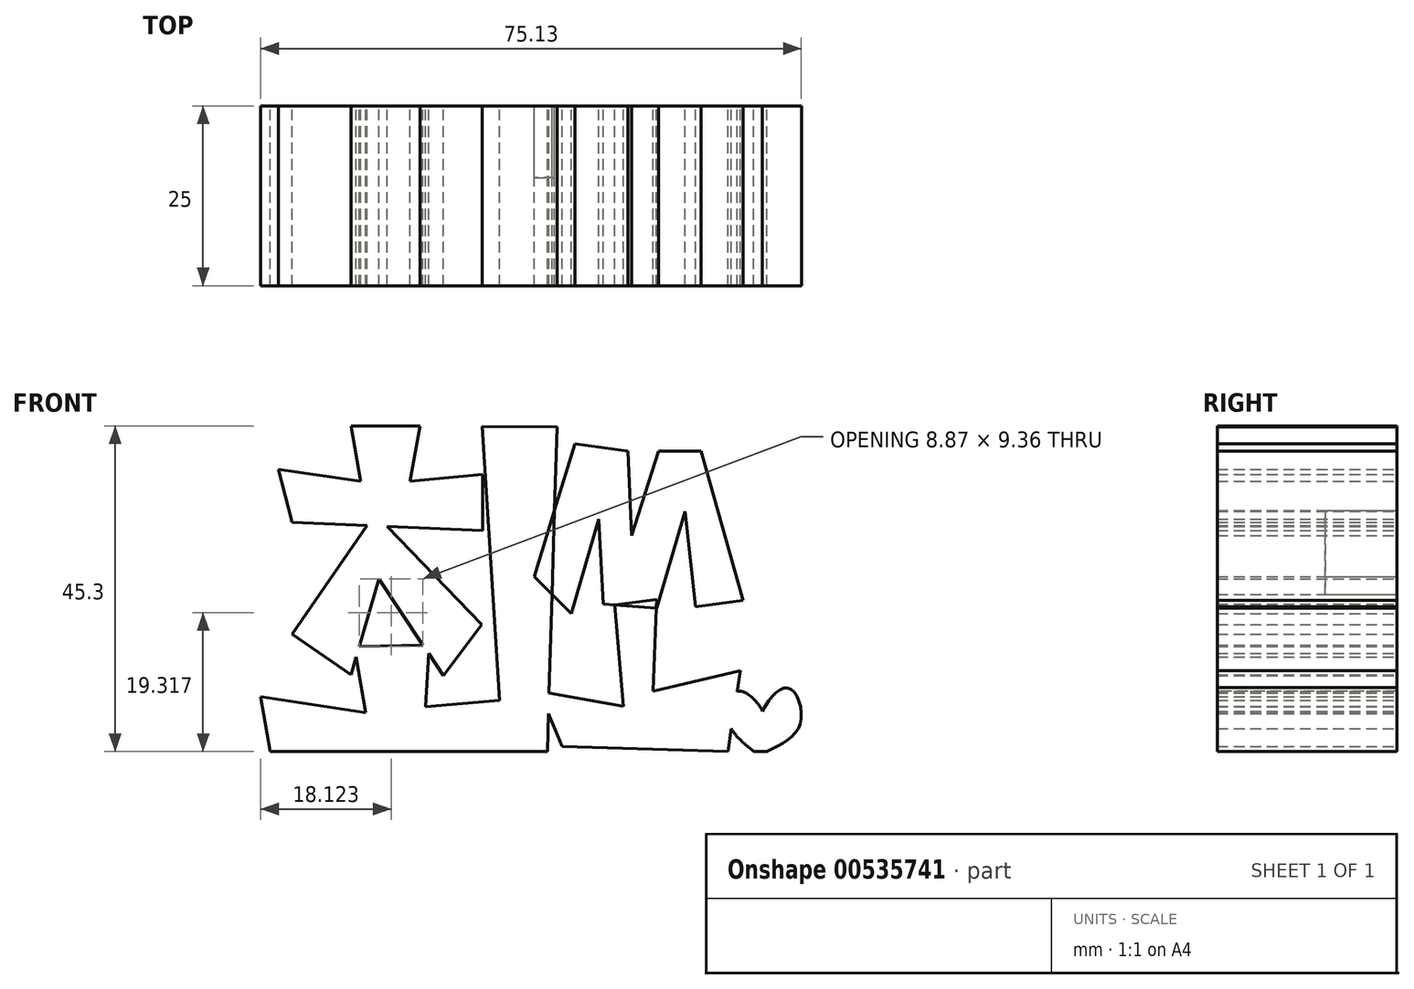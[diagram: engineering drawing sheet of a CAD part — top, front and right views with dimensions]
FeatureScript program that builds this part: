
annotation { "Feature Type Name" : "Feature", "Feature Type Description" : "" }
export const myFeature = defineFeature(function(context is Context, id is Id, definition is map)
    precondition{}
    {
        {
            var Q0;
            Q0=qCreatedBy(makeId("Front.planeOp"),FACE);
            var sketch = newSketch(context, id + "F0", { "sketchPlane" : qUnion([Q0])});
            skLineSegment(sketch, "E0", {"start": v(-41.35, 31.22) * mm, "end": v(-31.75, 31.22) * mm});
            skLineSegment(sketch, "E1", {"start": v(-31.75, 31.22) * mm, "end": v(-33.15, 23.5) * mm});
            skLineSegment(sketch, "E2", {"start": v(-33.15, 23.5) * mm, "end": v(-23.06, 24.46) * mm});
            skLineSegment(sketch, "E3", {"start": v(-23.06, 24.46) * mm, "end": v(-23.06, 16.67) * mm});
            skLineSegment(sketch, "E4", {"start": v(-23.06, 16.67) * mm, "end": v(-49.5, 17.8) * mm});
            skLineSegment(sketch, "E5", {"start": v(-49.5, 17.8) * mm, "end": v(-51.41, 25.15) * mm});
            skLineSegment(sketch, "E6", {"start": v(-51.41, 25.15) * mm, "end": v(-40, 23.5) * mm});
            skLineSegment(sketch, "E7", {"start": v(-40, 23.5) * mm, "end": v(-41.35, 31.22) * mm});
            skLineSegment(sketch, "E8", {"start": v(-39.09, 17.35) * mm, "end": v(-49.5, 2.24) * mm});
            skLineSegment(sketch, "E9", {"start": v(-49.5, 2.24) * mm, "end": v(-41.35, -3.39) * mm});
            skLineSegment(sketch, "E10", {"start": v(-41.35, -3.39) * mm, "end": v(-37.44, 9.92) * mm});
            skLineSegment(sketch, "E11", {"start": v(-37.44, 9.92) * mm, "end": v(-28.48, -3.52) * mm});
            skLineSegment(sketch, "E12", {"start": v(-28.48, -3.52) * mm, "end": v(-23.19, 3.56) * mm});
            skLineSegment(sketch, "E13", {"start": v(-23.19, 3.56) * mm, "end": v(-36.28, 17.23) * mm});
            skLineSegment(sketch, "E14", {"start": v(-40.63, -0.95) * mm, "end": v(-39.27, -8.71) * mm});
            skLineSegment(sketch, "E15", {"start": v(-39.27, -8.71) * mm, "end": v(-53.88, -6.46) * mm});
            skLineSegment(sketch, "E16", {"start": v(-53.88, -6.46) * mm, "end": v(-52.55, -14.08) * mm});
            skLineSegment(sketch, "E17", {"start": v(-52.55, -14.08) * mm, "end": v(-17.7, -14.08) * mm});
            skLineSegment(sketch, "E18", {"start": v(-17.7, -14.08) * mm, "end": v(-19.06, -6.8) * mm});
            skLineSegment(sketch, "E19", {"start": v(-19.06, -6.8) * mm, "end": v(-30.99, -7.88) * mm});
            skLineSegment(sketch, "E20", {"start": v(-30.99, -7.88) * mm, "end": v(-30.45, 0.76) * mm});
            skLineSegment(sketch, "E21", {"start": v(-30.45, 0.76) * mm, "end": v(-41.04, 0.54) * mm});
            skLineSegment(sketch, "E22", {"start": v(-41.04, 0.54) * mm, "end": v(-40.63, -0.95) * mm});
            skLineSegment(sketch, "E23", {"start": v(-23.12, 31.16) * mm, "end": v(-20.2, -14.08) * mm});
            skLineSegment(sketch, "E24", {"start": v(-20.2, -14.08) * mm, "end": v(-14.05, -14.08) * mm});
            skLineSegment(sketch, "E25", {"start": v(-14.05, -14.08) * mm, "end": v(-12.7, 31.07) * mm});
            skLineSegment(sketch, "E26", {"start": v(-12.7, 31.07) * mm, "end": v(-23.12, 31.16) * mm});
            skLineSegment(sketch, "E27", {"start": v(-10.2, 28.7) * mm, "end": v(-15.86, 10.26) * mm});
            skLineSegment(sketch, "E28", {"start": v(-15.86, 10.26) * mm, "end": v(-10.73, 5.12) * mm});
            skLineSegment(sketch, "E29", {"start": v(-10.73, 5.12) * mm, "end": v(-6.89, 18.24) * mm});
            skLineSegment(sketch, "E30", {"start": v(-6.89, 18.24) * mm, "end": v(-6.25, 6.4) * mm});
            skLineSegment(sketch, "E31", {"start": v(-6.25, 6.4) * mm, "end": v(1.14, 5.85) * mm});
            skLineSegment(sketch, "E32", {"start": v(1.14, 5.85) * mm, "end": v(5.08, 19.3) * mm});
            skLineSegment(sketch, "E33", {"start": v(5.08, 19.3) * mm, "end": v(6.55, 6.08) * mm});
            skLineSegment(sketch, "E34", {"start": v(6.55, 6.08) * mm, "end": v(13.16, 6.93) * mm});
            skLineSegment(sketch, "E35", {"start": v(13.16, 6.93) * mm, "end": v(7.3, 27.73) * mm});
            skLineSegment(sketch, "E36", {"start": v(7.3, 27.73) * mm, "end": v(1.43, 27.73) * mm});
            skLineSegment(sketch, "E37", {"start": v(1.43, 27.73) * mm, "end": v(-2.31, 15.93) * mm});
            skLineSegment(sketch, "E38", {"start": v(-2.31, 15.93) * mm, "end": v(-2.84, 27.73) * mm});
            skLineSegment(sketch, "E39", {"start": v(-2.84, 27.73) * mm, "end": v(-10.2, 28.7) * mm});
            skLineSegment(sketch, "E40", {"start": v(-4.67, 6.29) * mm, "end": v(1.14, 7.06) * mm});
            skLineSegment(sketch, "E41", {"start": v(1.14, 7.06) * mm, "end": v(0.67, -5.71) * mm});
            skLineSegment(sketch, "E42", {"start": v(0.67, -5.71) * mm, "end": v(12.76, -2.85) * mm});
            skLineSegment(sketch, "E43", {"start": v(12.76, -2.85) * mm, "end": v(11.05, -14.08) * mm});
            skLineSegment(sketch, "E44", {"start": v(11.05, -14.08) * mm, "end": v(-12, -13.38) * mm});
            skLineSegment(sketch, "E45", {"start": v(-12, -13.38) * mm, "end": v(-15.19, -5.71) * mm});
            skLineSegment(sketch, "E46", {"start": v(-15.19, -5.71) * mm, "end": v(-3.48, -7.79) * mm});
            skLineSegment(sketch, "E47", {"start": v(-3.48, -7.79) * mm, "end": v(-4.67, 6.29) * mm});
            skPoint(sketch, "E48.3.internal.snap0", {"position": v(11.9, -8.46) * mm});
            skFitSpline(sketch, "E48", {"points": [v(14.65, -14.08) * mm, v(11.05, -9.64) * mm, v(12.32, -5.74) * mm, v(15.85, -8.46) * mm, v(16.46, -14.08) * mm], "startDerivative": vector(-17.92, 14.39) * mm, "endDerivative": vector(-1.7, -21.54) * mm});
            skFitSpline(sketch, "E49", {"points": [v(14.65, -14.08) * mm, v(15.85, -8.46) * mm, v(19.47, -5.26) * mm, v(21.13, -10.1) * mm, v(16.46, -14.08) * mm], "startDerivative": vector(1.53, 21.63) * mm, "endDerivative": vector(-23.6, -11.26) * mm});
            skLineSegment(sketch, "E50", {"start": v(14.65, -14.08) * mm, "end": v(16.46, -14.08) * mm});
            skSolve(sketch);
        }
        {
            var Q0;
            {var subQ7=sQuery(id+"F0.wireOp",EDGE,"E42");Q0=makeQuery(id+"F0.imprint","IMPRINT",FACE,{"disambiguationData":[TD([[makeQuery(id+"F0.imprint","IMPRINT",EDGE,{"derivedFrom":subQ7}),-1.0]])]});}
            var Q1;
            {var subQ0=sQuery(id+"F0.wireOp",EDGE,"E48");var subQ1=sQuery(id+"F0.wireOp",EDGE,"E43");var subQ2=makeQuery(id+"F0.imprint","INTERSECT",VERTEX,{"disambiguationData":[OD(0.0)],"derivedFrom":[subQ1,subQ0]});Q1=makeQuery(id+"F0.imprint","IMPRINT",FACE,{"disambiguationData":[TD([[makeQuery(id+"F0.imprint","IMPRINT",EDGE,{"disambiguationData":[TD([[subQ2,-1.0]])],"derivedFrom":subQ1}),1.0]])]});}
            var Q2;
            {var subQ0=sQuery(id+"F0.wireOp",EDGE,"E50");Q2=makeQuery(id+"F0.imprint","IMPRINT",FACE,{"disambiguationData":[TD([[makeQuery(id+"F0.imprint","IMPRINT",EDGE,{"derivedFrom":subQ0}),1.0]])]});}
            var Q3;
            {var subQ0=sQuery(id+"F0.wireOp",EDGE,"E49");var subQ1=sQuery(id+"F0.wireOp",EDGE,"E48");var subQ3=makeQuery(id+"F0.imprint","INTERSECT",VERTEX,{"derivedFrom":[subQ1,subQ0]});Q3=makeQuery(id+"F0.imprint","IMPRINT",FACE,{"disambiguationData":[TD([[makeQuery(id+"F0.imprint","IMPRINT",EDGE,{"disambiguationData":[TD([[subQ3,-1.0]])],"derivedFrom":subQ1}),1.0]])]});}
            var Q4;
            {var subQ0=sQuery(id+"F0.wireOp",EDGE,"E48");var subQ1=sQuery(id+"F0.wireOp",EDGE,"E43");var subQ2=makeQuery(id+"F0.imprint","INTERSECT",VERTEX,{"disambiguationData":[OD(0.0)],"derivedFrom":[subQ1,subQ0]});Q4=makeQuery(id+"F0.imprint","IMPRINT",FACE,{"disambiguationData":[TD([[makeQuery(id+"F0.imprint","IMPRINT",EDGE,{"disambiguationData":[TD([[subQ2,-1.0]])],"derivedFrom":subQ1}),-1.0]])]});}
            var Q5;
            {var subQ13=sQuery(id+"F0.wireOp",EDGE,"E18");Q5=makeQuery(id+"F0.imprint","IMPRINT",FACE,{"disambiguationData":[TD([[makeQuery(id+"F0.imprint","IMPRINT",EDGE,{"derivedFrom":subQ13}),-1.0]])]});}
            var Q6;
            Q6=makeQuery(id+"F0.imprint","IMPRINT",FACE,{"disambiguationData":[TD([[makeQuery(id+"F0.imprint","IMPRINT",EDGE,{"derivedFrom":sQuery(id+"F0.wireOp",EDGE,"E0")}),-1.0]])]});
            var Q7;
            {var subQ7=sQuery(id+"F0.wireOp",EDGE,"E8");Q7=makeQuery(id+"F0.imprint","IMPRINT",FACE,{"disambiguationData":[TD([[makeQuery(id+"F0.imprint","IMPRINT",EDGE,{"derivedFrom":subQ7}),1.0]])]});}
            var Q8;
            {var subQ0=sQuery(id+"F0.wireOp",EDGE,"E14");Q8=makeQuery(id+"F0.imprint","IMPRINT",FACE,{"disambiguationData":[TD([[makeQuery(id+"F0.imprint","IMPRINT",EDGE,{"derivedFrom":subQ0}),1.0]])]});}
            var Q9;
            {var subQ0=sQuery(id+"F0.wireOp",EDGE,"E22");Q9=makeQuery(id+"F0.imprint","IMPRINT",FACE,{"disambiguationData":[TD([[makeQuery(id+"F0.imprint","IMPRINT",EDGE,{"derivedFrom":subQ0}),1.0]])]});}
            var Q10;
            {var subQ0=sQuery(id+"F0.wireOp",EDGE,"E20");var subQ1=sQuery(id+"F0.wireOp",EDGE,"E11");var subQ2=makeQuery(id+"F0.imprint","INTERSECT",VERTEX,{"derivedFrom":[subQ1,subQ0]});Q10=makeQuery(id+"F0.imprint","IMPRINT",FACE,{"disambiguationData":[TD([[makeQuery(id+"F0.imprint","IMPRINT",EDGE,{"disambiguationData":[TD([[subQ2,1.0]])],"derivedFrom":subQ1}),1.0]])]});}
            var Q11;
            {var subQ0=sQuery(id+"F0.wireOp",EDGE,"E18");Q11=makeQuery(id+"F0.imprint","IMPRINT",FACE,{"disambiguationData":[TD([[makeQuery(id+"F0.imprint","IMPRINT",EDGE,{"derivedFrom":subQ0}),1.0]])]});}
            var Q12;
            {var subQ0=sQuery(id+"F0.wireOp",EDGE,"E45");var subQ1=sQuery(id+"F0.wireOp",EDGE,"E25");var subQ2=makeQuery(id+"F0.imprint","INTERSECT",VERTEX,{"derivedFrom":[subQ1,subQ0]});Q12=makeQuery(id+"F0.imprint","IMPRINT",FACE,{"disambiguationData":[TD([[makeQuery(id+"F0.imprint","IMPRINT",EDGE,{"disambiguationData":[TD([[subQ2,-1.0]])],"derivedFrom":subQ1}),1.0]])]});}
            var Q13;
            {var subQ12=sQuery(id+"F0.wireOp",EDGE,"E29");Q13=makeQuery(id+"F0.imprint","IMPRINT",FACE,{"disambiguationData":[TD([[makeQuery(id+"F0.imprint","IMPRINT",EDGE,{"derivedFrom":subQ12}),1.0]])]});}
            extrude(context, id + "F1", {"entities" : qUnion([Q0, Q1, Q2, Q3, Q4, Q5, Q6, Q7, Q8, Q9, Q10, Q11, Q12, Q13]), "depth" : 25 * mm, "offsetDistance" : 25 * mm});
        }
        {
            var Q0;
            {var subQ0=sQuery(id+"F0.wireOp",EDGE,"E40");Q0=makeQuery(id+"F0.imprint","IMPRINT",FACE,{"disambiguationData":[TD([[makeQuery(id+"F0.imprint","IMPRINT",EDGE,{"derivedFrom":subQ0}),-1.0]])]});}
            extrude(context, id + "F2", {"entities" : qUnion([Q0]), "depth" : 25 * mm, "offsetDistance" : 25 * mm});
        }
        {
            var Q0;
            {var subQ0=sQuery(id+"F0.wireOp",EDGE,"E27");var subQ1=sQuery(id+"F0.wireOp",EDGE,"E25");var subQ2=makeQuery(id+"F0.imprint","INTERSECT",VERTEX,{"derivedFrom":[subQ1,subQ0]});Q0=makeQuery(id+"F0.imprint","IMPRINT",FACE,{"disambiguationData":[TD([[makeQuery(id+"F0.imprint","IMPRINT",EDGE,{"disambiguationData":[TD([[subQ2,1.0]])],"derivedFrom":subQ1}),1.0]])]});}
            extrude(context, id + "F3", {"entities" : qUnion([Q0]), "depth" : 10 * mm, "offsetDistance" : 25 * mm});
        }
    });
